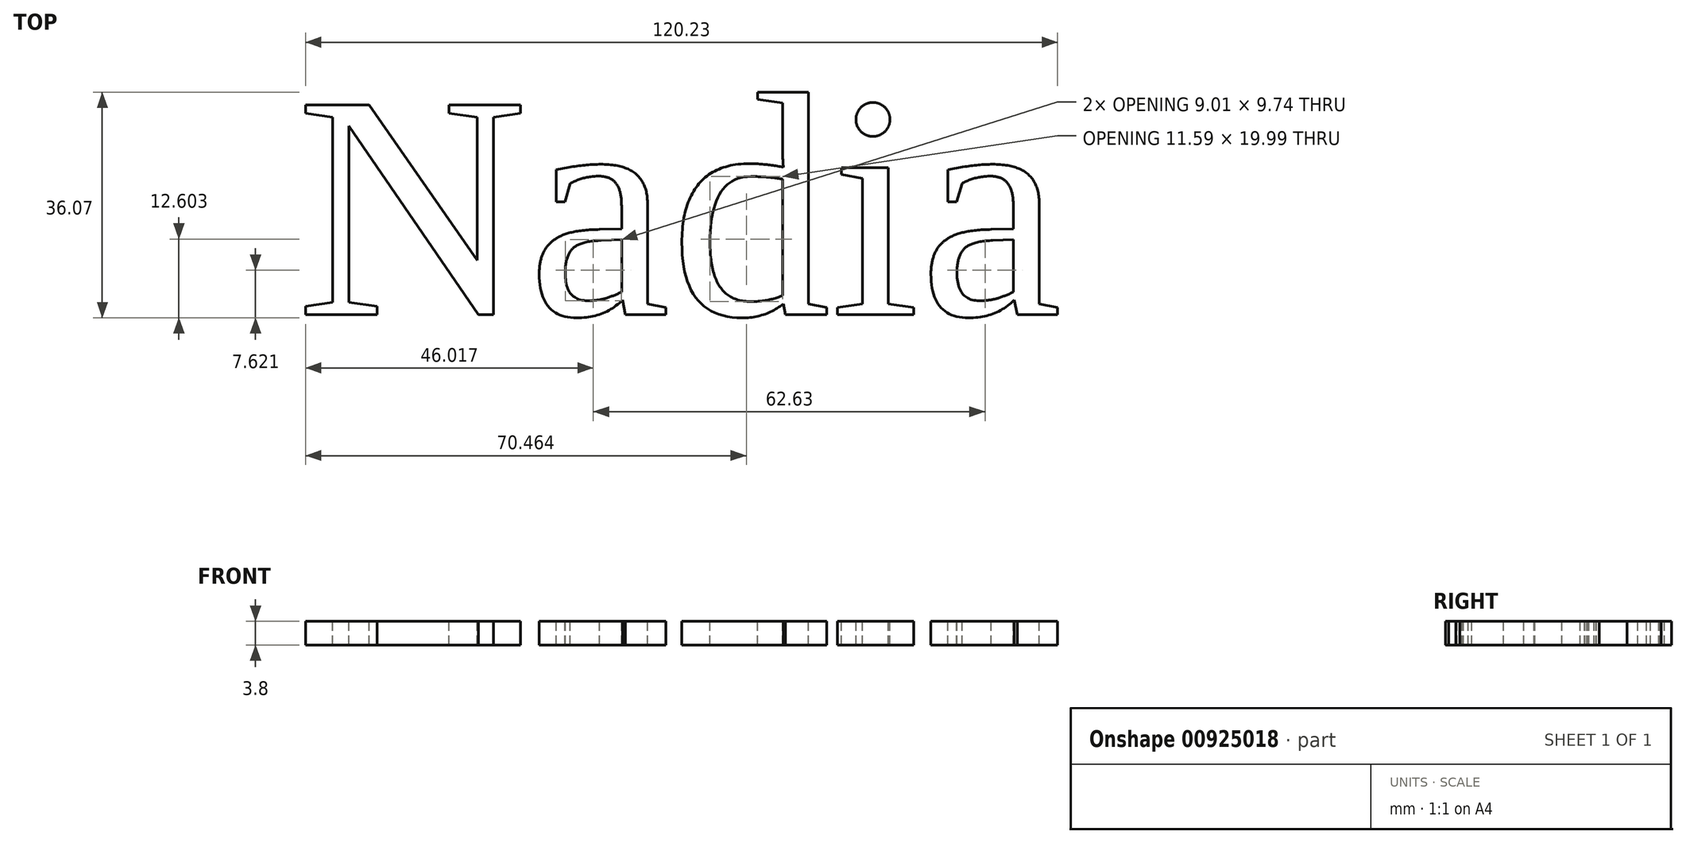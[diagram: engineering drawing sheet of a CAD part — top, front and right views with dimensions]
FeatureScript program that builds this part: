
annotation { "Feature Type Name" : "Feature", "Feature Type Description" : "" }
export const myFeature = defineFeature(function(context is Context, id is Id, definition is map)
    precondition{}
    {
        {
            var Q0;
            Q0=qCreatedBy(makeId("Top.planeOp"),FACE);
            var sketch = newSketch(context, id + "F0", { "sketchPlane" : qUnion([Q0])});
            skText(sketch, "E0", { "text": "Nadia", "fontName": "Tinos-Regular.ttf"});
            const initialGuessF0  = {"E0": [-0.0594, -0.01837, 1, 0, 0.03691]};
            skSetInitialGuess(sketch, initialGuessF0);
            skSolve(sketch);
        }
        {
            var Q0;
            Q0 = qSketchRegion(id + "F0", true);
            extrude(context, id + "F1", {"entities" : qUnion([Q0]), "oppositeDirection" : true, "depth" : 3.8 * mm, "offsetDistance" : 25 * mm});
        }
    });
